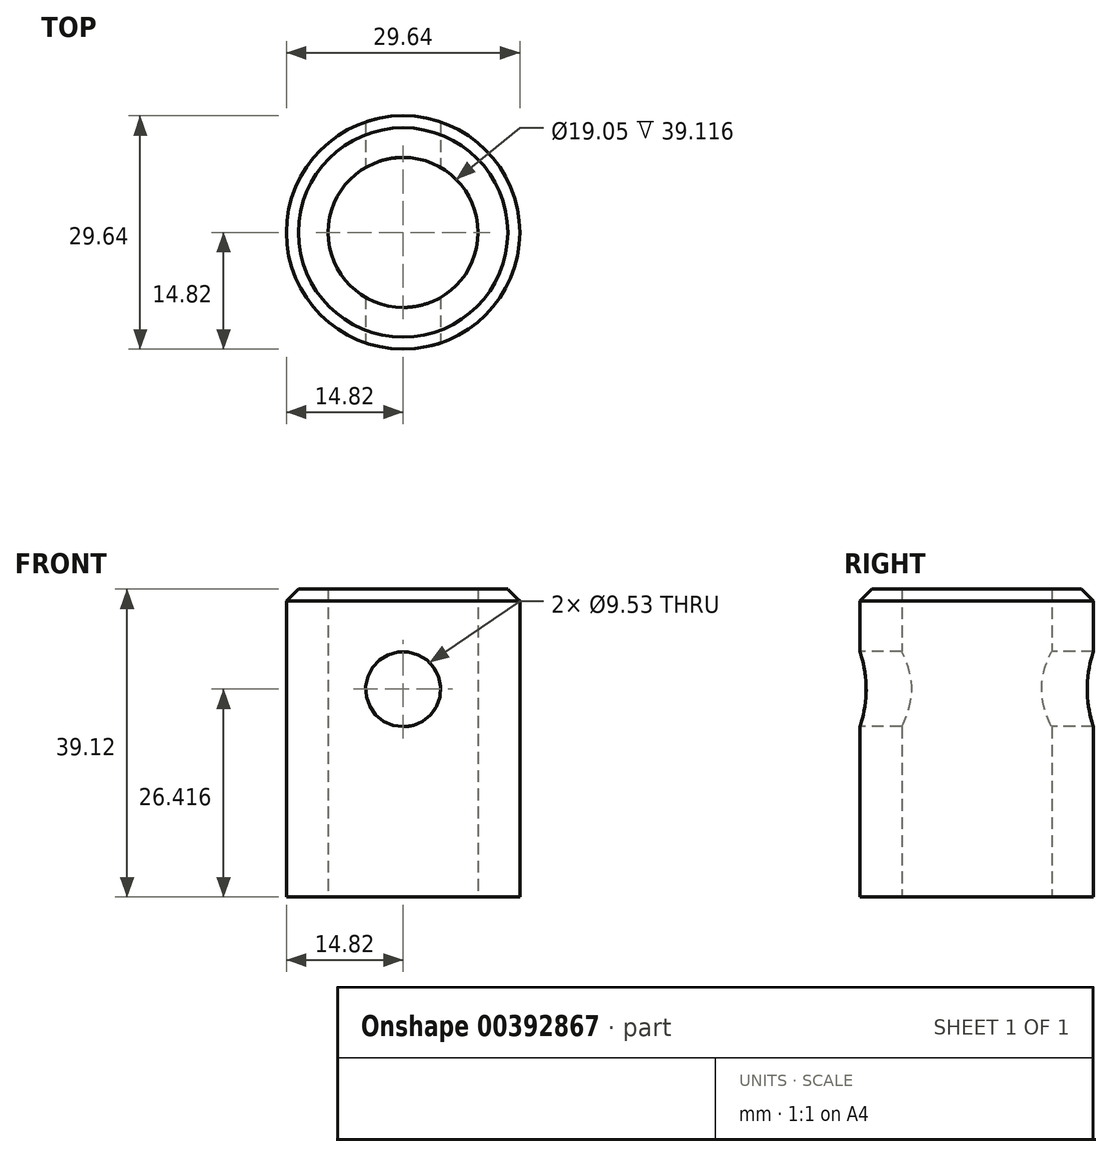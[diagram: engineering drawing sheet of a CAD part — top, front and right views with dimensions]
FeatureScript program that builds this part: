
annotation { "Feature Type Name" : "Feature", "Feature Type Description" : "" }
export const myFeature = defineFeature(function(context is Context, id is Id, definition is map)
    precondition{}
    {
        {
            var Q0;
            Q0=qCreatedBy(makeId("Top.planeOp"),FACE);
            var sketch = newSketch(context, id + "F0", { "sketchPlane" : qUnion([Q0])});
            skCircle(sketch, "E0", {"center": v(0, 0) * mm, "radius": 14.82 * mm});
            skCircle(sketch, "E1", {"center": v(0, 0) * mm, "radius": 9.53 * mm});
            skSolve(sketch);
        }
        {
            var Q0;
            Q0=makeQuery(id+"F0.imprint","IMPRINT",FACE,{"disambiguationData":[TD([[makeQuery(id+"F0.imprint","IMPRINT",EDGE,{"derivedFrom":sQuery(id+"F0.wireOp",EDGE,"E0")}),1.0]])]});
            extrude(context, id + "F1", {"entities" : qUnion([Q0]), "depth" : 39.12 * mm});
        }
        {
            var Q0;
            Q0=makeQuery(id+"F1.opExtrude","CAP_EDGE",EDGE,{"disambiguationData":[OSD([sQuery(id+"F0.wireOp",EDGE,"E0")])],"isStart":false});
            chamfer(context, id + "F2", {"entities" : qUnion([Q0]), "chamferType" : ChamferType.OFFSET_ANGLE, "width" : 1.52 * mm, "oppositeDirection" : false, "angle" : 45 * degree, "tangentPropagation" : true});
        }
        {
            var Q0;
            Q0=qCreatedBy(makeId("Front.planeOp"),FACE);
            cPlane(context, id + "F3", {"entities" : qUnion([Q0]), "cplaneType" : CPlaneType.OFFSET, "offset" : 14.82 * mm, "width" : 152.4 * mm, "height" : 152.4 * mm});
        }
        {
            var Q0;
            Q0=qCreatedBy(id+"F3.planeOp",FACE);
            var sketch = newSketch(context, id + "F4", { "sketchPlane" : qUnion([Q0])});
            skPoint(sketch, "E2", {"position": v(0, 26.42) * mm});
            skSolve(sketch);
        }
        {
            var Q0;
            Q0=sQuery(id+"F4.wireOp",VERTEX,"E2");
            var Q1;
            Q1=makeQuery(id+"F1.opExtrude","SWEPT_BODY",BODY,{"disambiguationData":[OSD([sQuery(id+"F0.wireOp",EDGE,"E0"),sQuery(id+"F0.wireOp",EDGE,"E1")])]});
            hole(context, id + "F5", {"style" : HoleStyle.SIMPLE, "endStyle" : HoleEndStyle.THROUGH, "holeDiameter" : 9.52 * mm, "isTappedThrough" : true, "tappedDepth" : 6.35 * mm, "tapClearance" : 3, "locations" : qUnion([Q0]), "scope" : qUnion([Q1])});
        }
    });
